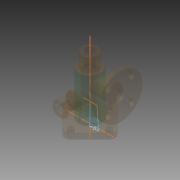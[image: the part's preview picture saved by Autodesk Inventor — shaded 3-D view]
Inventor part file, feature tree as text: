
AUTODESK INVENTOR PART (.ipt)
format: ipt  version: 2011 SP2 (Build 150309200, 309)  size: 269,824 bytes
history: native  units: mm
features: sketch x9, extrude x8, hole x4, plane x2, revolve x2, chamfer x1, projected_geometry x1
ambient origin geometry x8: Origin, YZ Plane, XZ Plane, XY Plane, X Axis, Y Axis, Z Axis, Center Point
bodies: Solid1 (feature_tree), Solid2 (feature_tree), Solid3 (feature_tree), Solid4 (feature_tree), Solid5 (feature_tree), Solid6 (feature_tree), Solid7 (feature_tree), Solid8 (feature_tree)
feature tree (27):
  extrude  "Extrusion1"  Depth=10.0mm
  extrude  "Extrusion2"  Depth=10.0mm
  extrude  "Extrusion3"  Depth=5.0mm
  plane  "Work Plane1"
  extrude  "Extrusion4"  Depth=40.0mm TaperAngle=360.0deg
  extrude  "Extrusion5"  Depth=20.0mm
  extrude  "Extrusion6"  Depth=15.0mm
  plane  "Work Plane2"
  extrude  "Extrusion7"  [1 undecoded]
  extrude  "Extrusion8"  Depth=50.0mm
  hole  "Hole3"  [1 undecoded]
  hole  "Hole4"  [1 undecoded]
  sketch  "Sketch10"  dims[d22=24.0mm d23=0.0mm d24=13.0mm d25=3.0mm d26=0.0mm d27=15.0mm d28=3.0mm d29=0.0mm d30=55.0mm d31=40.0mm d32=70.0mm d33=5.0mm d34=30.0mm d35=45.0deg d36=40.0mm d38=360.0deg d40=10.0mm d41=0.0mm d42=15.0mm d43=10.0mm d44=0.0mm d63=10.0mm d64=10.0mm d65=16.0mm d66=6.0mm d67=4.0mm d68=2.0mm d69=90.0deg d70=30.0mm d71=0.0mm d72=10.0mm d73=10.0mm d74=25.0mm d75=6.0mm d76=4.0mm d77=2.0mm d78=90.0deg d79=50.0mm d80=0.0mm d82=15.0mm d83=90.0deg d84=90.0deg d85=10.0mm d86=10.0mm d87=15.0mm d88=6.0mm d89=4.0mm d90=2.0mm d91=90.0deg d92=55.0mm d93=0.0mm d94=10.0mm d95=10.0mm d96=15.0mm d97=6.0mm d98=4.0mm d99=2.0mm d100=90.0deg d101=55.0mm d102=0.0mm d103=1.0mm d104=2.0mm d105=45.0deg]
  revolve  "Revolution1"  [1 undecoded]
  revolve  "Revolution2"  [1 undecoded]
  hole  "Hole5"  [1 undecoded]
  hole  "Hole6"  [1 undecoded]
  chamfer  "Chamfer1"  Distance=70.0mm
  sketch  "Sketch1"  dims[d0=70.0mm d1=10.0mm]
  sketch  "Sketch2"  dims[d2=10.0mm d3=10.0mm]
  sketch  "Sketch3"  dims[d4=10.0mm d5=5.0mm]
  sketch  "Sketch4"  dims[d6=35.0mm d7=40.0mm d9=360.0deg]
  sketch  "Sketch5"  dims[d11=10.0mm d12=0.0mm d13=20.0mm]
  sketch  "Sketch6"  dims[d14=80.0mm d15=0.0mm d16=15.0mm]
  sketch  "Sketch7"  dims[d17=25.0mm d18=0.0mm d19=-55.0mm]
  sketch  "Sketch8"  dims[d20=13.5mm d21=50.0mm]
  projected_geometry  "Projected Loop1"
note: 7 required parameter values undecoded (feature->parameter linkage not recoverable at this tier; creation-order binding heuristic only, values carry confidence <= 0.55)